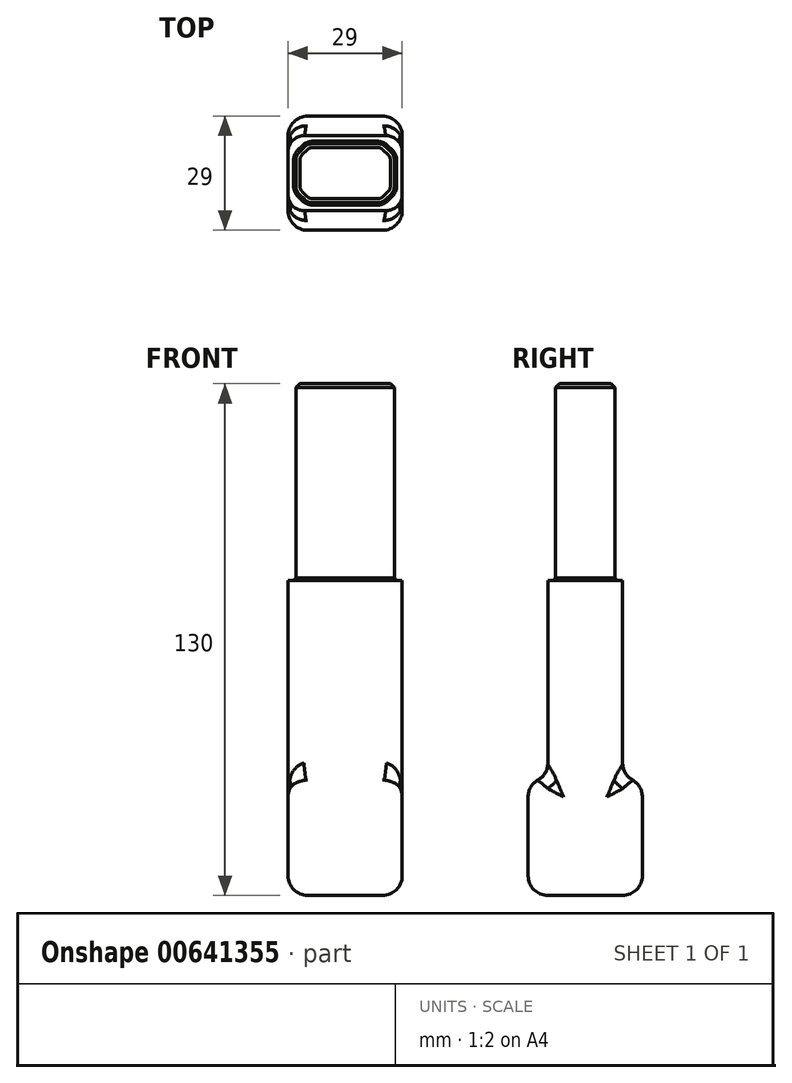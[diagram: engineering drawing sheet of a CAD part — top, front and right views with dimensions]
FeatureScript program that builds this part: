
annotation { "Feature Type Name" : "Feature", "Feature Type Description" : "" }
export const myFeature = defineFeature(function(context is Context, id is Id, definition is map)
    precondition{}
    {
        {
            var Q0;
            Q0=qCreatedBy(makeId("Top.planeOp"),FACE);
            var sketch = newSketch(context, id + "F0", { "sketchPlane" : qUnion([Q0])});
            skLineSegment(sketch, "E0.bottom", {"start": v(-12.5, 7.5) * mm, "end": v(12.5, 7.5) * mm});
            skLineSegment(sketch, "E0.top", {"start": v(-12.5, -7.5) * mm, "end": v(12.5, -7.5) * mm});
            skLineSegment(sketch, "E0.left", {"start": v(-12.5, 7.5) * mm, "end": v(-12.5, -7.5) * mm});
            skLineSegment(sketch, "E0.right", {"start": v(12.5, 7.5) * mm, "end": v(12.5, -7.5) * mm});
            skPoint(sketch, "E0.middle", {"position": v(0, 0) * mm});
            skLineSegment(sketch, "E1.0", {"start": v(-14.5, 9.5) * mm, "end": v(-14.5, -9.5) * mm});
            skLineSegment(sketch, "E1.1", {"start": v(-14.5, 9.5) * mm, "end": v(14.5, 9.5) * mm});
            skLineSegment(sketch, "E1.2", {"start": v(14.5, 9.5) * mm, "end": v(14.5, -9.5) * mm});
            skLineSegment(sketch, "E1.3", {"start": v(-14.5, -9.5) * mm, "end": v(14.5, -9.5) * mm});
            skSolve(sketch);
        }
        {
            var Q0;
            Q0 = qSketchRegion(id + "F0", true);
            var Q1;
            Q1=makeQuery(id+"F0.imprint","IMPRINT",FACE,{"disambiguationData":[TD([[makeQuery(id+"F0.imprint","IMPRINT",EDGE,{"derivedFrom":sQuery(id+"F0.wireOp",EDGE,"E0.bottom")}),-1.0]])]});
            extrude(context, id + "F1", {"entities" : qUnion([Q0, Q1]), "depth" : 80 * mm, "offsetDistance" : 25 * mm});
        }
        {
            var Q0;
            Q0=makeQuery(id+"F0.imprint","IMPRINT",FACE,{"disambiguationData":[TD([[makeQuery(id+"F0.imprint","IMPRINT",EDGE,{"derivedFrom":sQuery(id+"F0.wireOp",EDGE,"E0.bottom")}),-1.0]])]});
            extrude(context, id + "F2", {"entities" : qUnion([Q0]), "operationType" : NewBodyOperationType.ADD, "depth" : 130 * mm, "offsetDistance" : 25 * mm});
        }
        {
            var Q0;
            Q0=makeQuery(id+"F2.opExtrude","SWEPT_EDGE",EDGE,{"disambiguationData":[OSD([sQuery(id+"F0.wireOp",EDGE,"E0.bottom"),sQuery(id+"F0.wireOp",EDGE,"E0.right")])]});
            var Q1;
            Q1=makeQuery(id+"F2.opExtrude","SWEPT_EDGE",EDGE,{"disambiguationData":[OSD([sQuery(id+"F0.wireOp",EDGE,"E0.top"),sQuery(id+"F0.wireOp",EDGE,"E0.right")])]});
            var Q2;
            Q2=makeQuery(id+"F2.opExtrude","SWEPT_EDGE",EDGE,{"disambiguationData":[OSD([sQuery(id+"F0.wireOp",EDGE,"E0.bottom"),sQuery(id+"F0.wireOp",EDGE,"E0.left")])]});
            var Q3;
            Q3=makeQuery(id+"F2.opExtrude","SWEPT_EDGE",EDGE,{"disambiguationData":[OSD([sQuery(id+"F0.wireOp",EDGE,"E0.top"),sQuery(id+"F0.wireOp",EDGE,"E0.left")])]});
            chamfer(context, id + "F3", {"entities" : qUnion([Q0, Q1, Q2, Q3]), "width" : 3 * mm, "tangentPropagation" : true});
        }
        {
            var Q0;
            {var subQ0=sQuery(id+"F0.wireOp",EDGE,"E0.top");Q0=makeQuery(id+"F3.opChamfer","BLEND_EDGE",EDGE,{"blendedFrom":[makeQuery(id+"F2.opExtrude","SWEPT_EDGE",EDGE,{"disambiguationData":[OSD([subQ0,sQuery(id+"F0.wireOp",EDGE,"E0.left")])]}),makeQuery(id+"F2.opExtrude","SWEPT_FACE",FACE,{"disambiguationData":[OSD([subQ0])]})],"blendedInto":[makeQuery(id+"F2.opExtrude","SWEPT_FACE",FACE,{"disambiguationData":[OSD([subQ0])]})]});}
            var Q1;
            {var subQ0=sQuery(id+"F0.wireOp",EDGE,"E0.top");Q1=makeQuery(id+"F3.opChamfer","BLEND_EDGE",EDGE,{"blendedFrom":[makeQuery(id+"F2.opExtrude","SWEPT_EDGE",EDGE,{"disambiguationData":[OSD([subQ0,sQuery(id+"F0.wireOp",EDGE,"E0.right")])]}),makeQuery(id+"F2.opExtrude","SWEPT_FACE",FACE,{"disambiguationData":[OSD([subQ0])]})],"blendedInto":[makeQuery(id+"F2.opExtrude","SWEPT_FACE",FACE,{"disambiguationData":[OSD([subQ0])]})]});}
            var Q2;
            {var subQ0=sQuery(id+"F0.wireOp",EDGE,"E0.right");Q2=makeQuery(id+"F3.opChamfer","BLEND_EDGE",EDGE,{"blendedFrom":[makeQuery(id+"F2.opExtrude","SWEPT_EDGE",EDGE,{"disambiguationData":[OSD([sQuery(id+"F0.wireOp",EDGE,"E0.top"),subQ0])]}),makeQuery(id+"F2.opExtrude","SWEPT_FACE",FACE,{"disambiguationData":[OSD([subQ0])]})],"blendedInto":[makeQuery(id+"F2.opExtrude","SWEPT_FACE",FACE,{"disambiguationData":[OSD([subQ0])]})]});}
            var Q3;
            {var subQ0=sQuery(id+"F0.wireOp",EDGE,"E0.right");Q3=makeQuery(id+"F3.opChamfer","BLEND_EDGE",EDGE,{"blendedFrom":[makeQuery(id+"F2.opExtrude","SWEPT_EDGE",EDGE,{"disambiguationData":[OSD([sQuery(id+"F0.wireOp",EDGE,"E0.bottom"),subQ0])]}),makeQuery(id+"F2.opExtrude","SWEPT_FACE",FACE,{"disambiguationData":[OSD([subQ0])]})],"blendedInto":[makeQuery(id+"F2.opExtrude","SWEPT_FACE",FACE,{"disambiguationData":[OSD([subQ0])]})]});}
            var Q4;
            {var subQ0=sQuery(id+"F0.wireOp",EDGE,"E0.bottom");Q4=makeQuery(id+"F3.opChamfer","BLEND_EDGE",EDGE,{"blendedFrom":[makeQuery(id+"F2.opExtrude","SWEPT_EDGE",EDGE,{"disambiguationData":[OSD([subQ0,sQuery(id+"F0.wireOp",EDGE,"E0.right")])]}),makeQuery(id+"F2.opExtrude","SWEPT_FACE",FACE,{"disambiguationData":[OSD([subQ0])]})],"blendedInto":[makeQuery(id+"F2.opExtrude","SWEPT_FACE",FACE,{"disambiguationData":[OSD([subQ0])]})]});}
            var Q5;
            {var subQ0=sQuery(id+"F0.wireOp",EDGE,"E0.left");Q5=makeQuery(id+"F3.opChamfer","BLEND_EDGE",EDGE,{"blendedFrom":[makeQuery(id+"F2.opExtrude","SWEPT_EDGE",EDGE,{"disambiguationData":[OSD([sQuery(id+"F0.wireOp",EDGE,"E0.top"),subQ0])]}),makeQuery(id+"F2.opExtrude","SWEPT_FACE",FACE,{"disambiguationData":[OSD([subQ0])]})],"blendedInto":[makeQuery(id+"F2.opExtrude","SWEPT_FACE",FACE,{"disambiguationData":[OSD([subQ0])]})]});}
            var Q6;
            {var subQ0=sQuery(id+"F0.wireOp",EDGE,"E0.left");Q6=makeQuery(id+"F3.opChamfer","BLEND_EDGE",EDGE,{"blendedFrom":[makeQuery(id+"F2.opExtrude","SWEPT_EDGE",EDGE,{"disambiguationData":[OSD([sQuery(id+"F0.wireOp",EDGE,"E0.bottom"),subQ0])]}),makeQuery(id+"F2.opExtrude","SWEPT_FACE",FACE,{"disambiguationData":[OSD([subQ0])]})],"blendedInto":[makeQuery(id+"F2.opExtrude","SWEPT_FACE",FACE,{"disambiguationData":[OSD([subQ0])]})]});}
            var Q7;
            {var subQ0=sQuery(id+"F0.wireOp",EDGE,"E0.bottom");Q7=makeQuery(id+"F3.opChamfer","BLEND_EDGE",EDGE,{"blendedFrom":[makeQuery(id+"F2.opExtrude","SWEPT_EDGE",EDGE,{"disambiguationData":[OSD([subQ0,sQuery(id+"F0.wireOp",EDGE,"E0.left")])]}),makeQuery(id+"F2.opExtrude","SWEPT_FACE",FACE,{"disambiguationData":[OSD([subQ0])]})],"blendedInto":[makeQuery(id+"F2.opExtrude","SWEPT_FACE",FACE,{"disambiguationData":[OSD([subQ0])]})]});}
            fillet(context, id + "F4", {"entities" : qUnion([Q0, Q1, Q2, Q3, Q4, Q5, Q6, Q7]), "radius" : 3 * mm, "tangentPropagation" : true, "allowEdgeOverflow" : false});
        }
        {
            var Q0;
            Q0=makeQuery(id+"F1.opExtrude","SWEPT_EDGE",EDGE,{"disambiguationData":[OSD([sQuery(id+"F0.wireOp",EDGE,"E1.2"),sQuery(id+"F0.wireOp",EDGE,"E1.3")])]});
            var Q1;
            Q1=makeQuery(id+"F1.opExtrude","SWEPT_EDGE",EDGE,{"disambiguationData":[OSD([sQuery(id+"F0.wireOp",EDGE,"E1.1"),sQuery(id+"F0.wireOp",EDGE,"E1.2")])]});
            var Q2;
            Q2=makeQuery(id+"F1.opExtrude","SWEPT_EDGE",EDGE,{"disambiguationData":[OSD([sQuery(id+"F0.wireOp",EDGE,"E1.0"),sQuery(id+"F0.wireOp",EDGE,"E1.3")])]});
            var Q3;
            Q3=makeQuery(id+"F1.opExtrude","SWEPT_EDGE",EDGE,{"disambiguationData":[OSD([sQuery(id+"F0.wireOp",EDGE,"E1.0"),sQuery(id+"F0.wireOp",EDGE,"E1.1")])]});
            fillet(context, id + "F5", {"entities" : qUnion([Q0, Q1, Q2, Q3]), "radius" : 4 * mm, "tangentPropagation" : true, "allowEdgeOverflow" : false});
        }
        {
            var Q0;
            Q0=makeQuery(id+"F2.boolean.opBoolean","INTERSECT",EDGE,{"derivedFrom":[makeQuery(id+"F1.opExtrude","CAP_FACE",FACE,{"disambiguationData":[OSD([sQuery(id+"F0.wireOp",EDGE,"E1.0"),sQuery(id+"F0.wireOp",EDGE,"E1.1"),sQuery(id+"F0.wireOp",EDGE,"E1.2"),sQuery(id+"F0.wireOp",EDGE,"E1.3")])],"isStart":false}),makeQuery(id+"F2.opExtrude","SWEPT_FACE",FACE,{"disambiguationData":[OSD([sQuery(id+"F0.wireOp",EDGE,"E0.top")])]})]});
            chamfer(context, id + "F6", {"entities" : qUnion([Q0]), "width" : 0.6 * mm, "tangentPropagation" : true});
        }
        {
            var Q0;
            Q0=makeQuery(id+"F2.opExtrude","CAP_EDGE",EDGE,{"disambiguationData":[OSD([sQuery(id+"F0.wireOp",EDGE,"E0.top")])],"isStart":false});
            chamfer(context, id + "F7", {"entities" : qUnion([Q0]), "width" : 1 * mm, "tangentPropagation" : true});
        }
        {
            var Q0;
            Q0=qCreatedBy(makeId("Top.planeOp"),FACE);
            var sketch = newSketch(context, id + "F8", { "sketchPlane" : qUnion([Q0])});
            skPoint(sketch, "E2.middle", {"position": v(0, 0) * mm});
            skPoint(sketch, "E3.visualSharp", {"position": v(-30, 24.5) * mm});
            skPoint(sketch, "E4.visualSharp", {"position": v(30, -24.5) * mm});
            skPoint(sketch, "E5.visualSharp", {"position": v(-30, -24.5) * mm});
            skLineSegment(sketch, "E6.bottom", {"start": v(14.5, 14.5) * mm, "end": v(-14.5, 14.5) * mm});
            skLineSegment(sketch, "E6.top", {"start": v(14.5, -14.5) * mm, "end": v(-14.5, -14.5) * mm});
            skLineSegment(sketch, "E6.left", {"start": v(14.5, 14.5) * mm, "end": v(14.5, -14.5) * mm});
            skLineSegment(sketch, "E6.right", {"start": v(-14.5, 14.5) * mm, "end": v(-14.5, -14.5) * mm});
            skSolve(sketch);
        }
        {
            var Q0;
            Q0=makeQuery(id+"F8.imprint","IMPRINT",FACE,{"disambiguationData":[TD([[makeQuery(id+"F8.imprint","IMPRINT",EDGE,{"derivedFrom":sQuery(id+"F8.wireOp",EDGE,"E6.bottom")}),1.0]])]});
            extrude(context, id + "F9", {"entities" : qUnion([Q0]), "operationType" : NewBodyOperationType.ADD, "depth" : 30 * mm, "offsetDistance" : 25 * mm});
        }
        {
            var Q0;
            Q0=makeQuery(id+"F9.opExtrude","SWEPT_EDGE",EDGE,{"disambiguationData":[OSD([sQuery(id+"F8.wireOp",EDGE,"E6.top"),sQuery(id+"F8.wireOp",EDGE,"E6.right")])]});
            var Q1;
            Q1=makeQuery(id+"F9.opExtrude","SWEPT_EDGE",EDGE,{"disambiguationData":[OSD([sQuery(id+"F8.wireOp",EDGE,"E6.top"),sQuery(id+"F8.wireOp",EDGE,"E6.left")])]});
            var Q2;
            Q2=makeQuery(id+"F9.opExtrude","SWEPT_EDGE",EDGE,{"disambiguationData":[OSD([sQuery(id+"F8.wireOp",EDGE,"E6.bottom"),sQuery(id+"F8.wireOp",EDGE,"E6.left")])]});
            var Q3;
            Q3=makeQuery(id+"F9.opExtrude","SWEPT_EDGE",EDGE,{"disambiguationData":[OSD([sQuery(id+"F8.wireOp",EDGE,"E6.bottom"),sQuery(id+"F8.wireOp",EDGE,"E6.right")])]});
            fillet(context, id + "F10", {"entities" : qUnion([Q0, Q1, Q2, Q3]), "radius" : 5 * mm, "tangentPropagation" : true, "allowEdgeOverflow" : false});
        }
        {
            var Q0;
            Q0=makeQuery(id+"F9.opExtrude","CAP_EDGE",EDGE,{"disambiguationData":[OSD([sQuery(id+"F8.wireOp",EDGE,"E6.bottom")])],"isStart":false});
            var Q1;
            {var subQ0=sQuery(id+"F0.wireOp",EDGE,"E1.3");var subQ3=sQuery(id+"F8.wireOp",EDGE,"E6.top");var subQ4=sQuery(id+"F8.wireOp",EDGE,"E6.left");var subQ5=sQuery(id+"F8.wireOp",EDGE,"E6.right");Q1=makeQuery(id+"F10.opFillet","BLEND_EDGE",EDGE,{"blendedFrom":[makeQuery(id+"F9.opExtrude","SWEPT_EDGE",EDGE,{"disambiguationData":[OSD([subQ3,subQ5])]}),makeQuery(id+"F9.boolean.opBoolean","SPLIT",FACE,{"disambiguationData":[TD([makeQuery(id+"F1.opExtrude","SWEPT_FACE",FACE,{"disambiguationData":[OSD([subQ0])]})])],"derivedFrom":makeQuery(id+"F9.opExtrude","CAP_FACE",FACE,{"disambiguationData":[OSD([sQuery(id+"F8.wireOp",EDGE,"E6.bottom"),subQ3,subQ4,subQ5])],"isStart":false})})],"blendedInto":[makeQuery(id+"F9.boolean.opBoolean","SPLIT",FACE,{"disambiguationData":[TD([makeQuery(id+"F1.opExtrude","SWEPT_FACE",FACE,{"disambiguationData":[OSD([subQ0])]})])],"derivedFrom":makeQuery(id+"F9.opExtrude","CAP_FACE",FACE,{"disambiguationData":[OSD([sQuery(id+"F8.wireOp",EDGE,"E6.bottom"),subQ3,subQ4,subQ5])],"isStart":false})})]});}
            var Q2;
            {var subQ0=sQuery(id+"F8.wireOp",EDGE,"E6.right");var subQ1=sQuery(id+"F8.wireOp",EDGE,"E6.bottom");Q2=makeQuery(id+"F10.opFillet","BLEND_EDGE",EDGE,{"blendedFrom":[makeQuery(id+"F9.opExtrude","SWEPT_EDGE",EDGE,{"disambiguationData":[OSD([subQ1,subQ0])]}),makeQuery(id+"F9.boolean.opBoolean","MERGE",FACE,{"derivedFrom":[makeQuery(id+"F1.opExtrude","CAP_FACE",FACE,{"disambiguationData":[OSD([sQuery(id+"F0.wireOp",EDGE,"E1.0"),sQuery(id+"F0.wireOp",EDGE,"E1.1"),sQuery(id+"F0.wireOp",EDGE,"E1.2"),sQuery(id+"F0.wireOp",EDGE,"E1.3")])],"isStart":true}),makeQuery(id+"F9.opExtrude","CAP_FACE",FACE,{"disambiguationData":[OSD([subQ1,sQuery(id+"F8.wireOp",EDGE,"E6.top"),sQuery(id+"F8.wireOp",EDGE,"E6.left"),subQ0])],"isStart":true})]})],"blendedInto":[makeQuery(id+"F9.boolean.opBoolean","MERGE",FACE,{"derivedFrom":[makeQuery(id+"F1.opExtrude","CAP_FACE",FACE,{"disambiguationData":[OSD([sQuery(id+"F0.wireOp",EDGE,"E1.0"),sQuery(id+"F0.wireOp",EDGE,"E1.1"),sQuery(id+"F0.wireOp",EDGE,"E1.2"),sQuery(id+"F0.wireOp",EDGE,"E1.3")])],"isStart":true}),makeQuery(id+"F9.opExtrude","CAP_FACE",FACE,{"disambiguationData":[OSD([subQ1,sQuery(id+"F8.wireOp",EDGE,"E6.top"),sQuery(id+"F8.wireOp",EDGE,"E6.left"),subQ0])],"isStart":true})]})]});}
            fillet(context, id + "F11", {"entities" : qUnion([Q0, Q1, Q2]), "radius" : 5 * mm, "tangentPropagation" : true, "allowEdgeOverflow" : false});
        }
        {
            var Q0;
            Q0=makeQuery(id+"F11.opFillet","BLEND_EDGE",EDGE,{"blendedFrom":[makeQuery(id+"F9.opExtrude","CAP_EDGE",EDGE,{"disambiguationData":[OSD([sQuery(id+"F8.wireOp",EDGE,"E6.bottom")])],"isStart":false}),makeQuery(id+"F1.opExtrude","SWEPT_FACE",FACE,{"disambiguationData":[OSD([sQuery(id+"F0.wireOp",EDGE,"E1.1")])]})],"blendedInto":[makeQuery(id+"F1.opExtrude","SWEPT_FACE",FACE,{"disambiguationData":[OSD([sQuery(id+"F0.wireOp",EDGE,"E1.1")])]})]});
            var Q1;
            Q1=makeQuery(id+"F11.opFillet","BLEND_EDGE",EDGE,{"blendedFrom":[makeQuery(id+"F9.opExtrude","CAP_EDGE",EDGE,{"disambiguationData":[OSD([sQuery(id+"F8.wireOp",EDGE,"E6.top")])],"isStart":false}),makeQuery(id+"F1.opExtrude","SWEPT_FACE",FACE,{"disambiguationData":[OSD([sQuery(id+"F0.wireOp",EDGE,"E1.3")])]})],"blendedInto":[makeQuery(id+"F1.opExtrude","SWEPT_FACE",FACE,{"disambiguationData":[OSD([sQuery(id+"F0.wireOp",EDGE,"E1.3")])]})]});
            fillet(context, id + "F12", {"entities" : qUnion([Q0, Q1]), "radius" : 5 * mm, "tangentPropagation" : true, "allowEdgeOverflow" : false});
        }
    });
